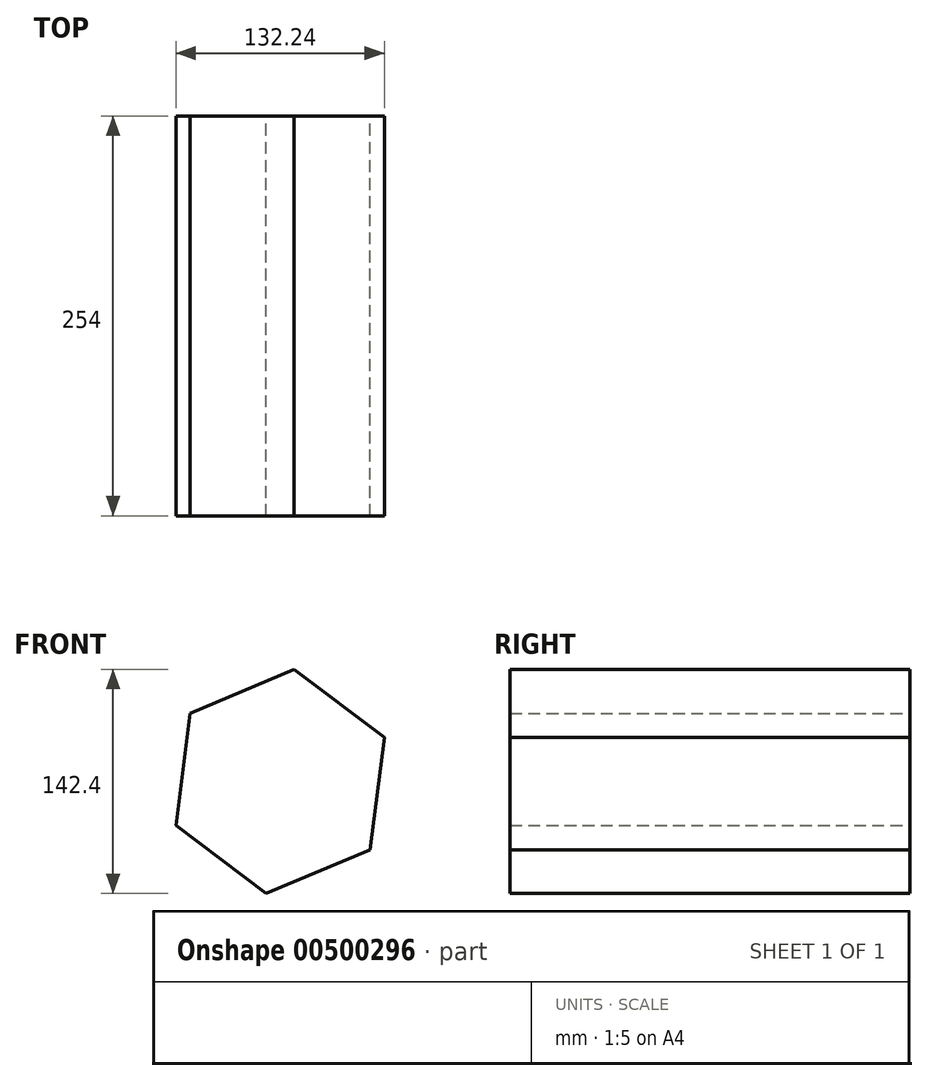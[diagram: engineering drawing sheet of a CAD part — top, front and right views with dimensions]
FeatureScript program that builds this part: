
annotation { "Feature Type Name" : "Feature", "Feature Type Description" : "" }
export const myFeature = defineFeature(function(context is Context, id is Id, definition is map)
    precondition{}
    {
        {
            var Q0;
            Q0=qCreatedBy(makeId("Front.planeOp"),FACE);
            var sketch = newSketch(context, id + "F0", { "sketchPlane" : qUnion([Q0])});
            skCircle(sketch, "E0.cCircle", {"center": v(0, 0) * mm, "radius": 71.75 * mm, "construction": true});
            skLineSegment(sketch, "E0.0", {"start": v(-57.2, 43.32) * mm, "end": v(8.91, 71.2) * mm});
            skLineSegment(sketch, "E0.1", {"start": v(8.91, 71.2) * mm, "end": v(66.12, 27.88) * mm});
            skLineSegment(sketch, "E0.2", {"start": v(66.12, 27.88) * mm, "end": v(57.2, -43.32) * mm});
            skLineSegment(sketch, "E0.3", {"start": v(57.2, -43.32) * mm, "end": v(-8.91, -71.2) * mm});
            skLineSegment(sketch, "E0.4", {"start": v(-8.91, -71.2) * mm, "end": v(-66.12, -27.88) * mm});
            skLineSegment(sketch, "E0.5", {"start": v(-66.12, -27.88) * mm, "end": v(-57.2, 43.32) * mm});
            skSolve(sketch);
        }
        {
            var Q0;
            Q0=makeQuery(id+"F0.imprint","IMPRINT",FACE,{"disambiguationData":[TD([[makeQuery(id+"F0.imprint","IMPRINT",EDGE,{"derivedFrom":sQuery(id+"F0.wireOp",EDGE,"E0.0")}),-1.0]])]});
            extrude(context, id + "F1", {"entities" : qUnion([Q0]), "endBound" : BoundingType.SYMMETRIC, "depth" : 254 * mm});
        }
    });
